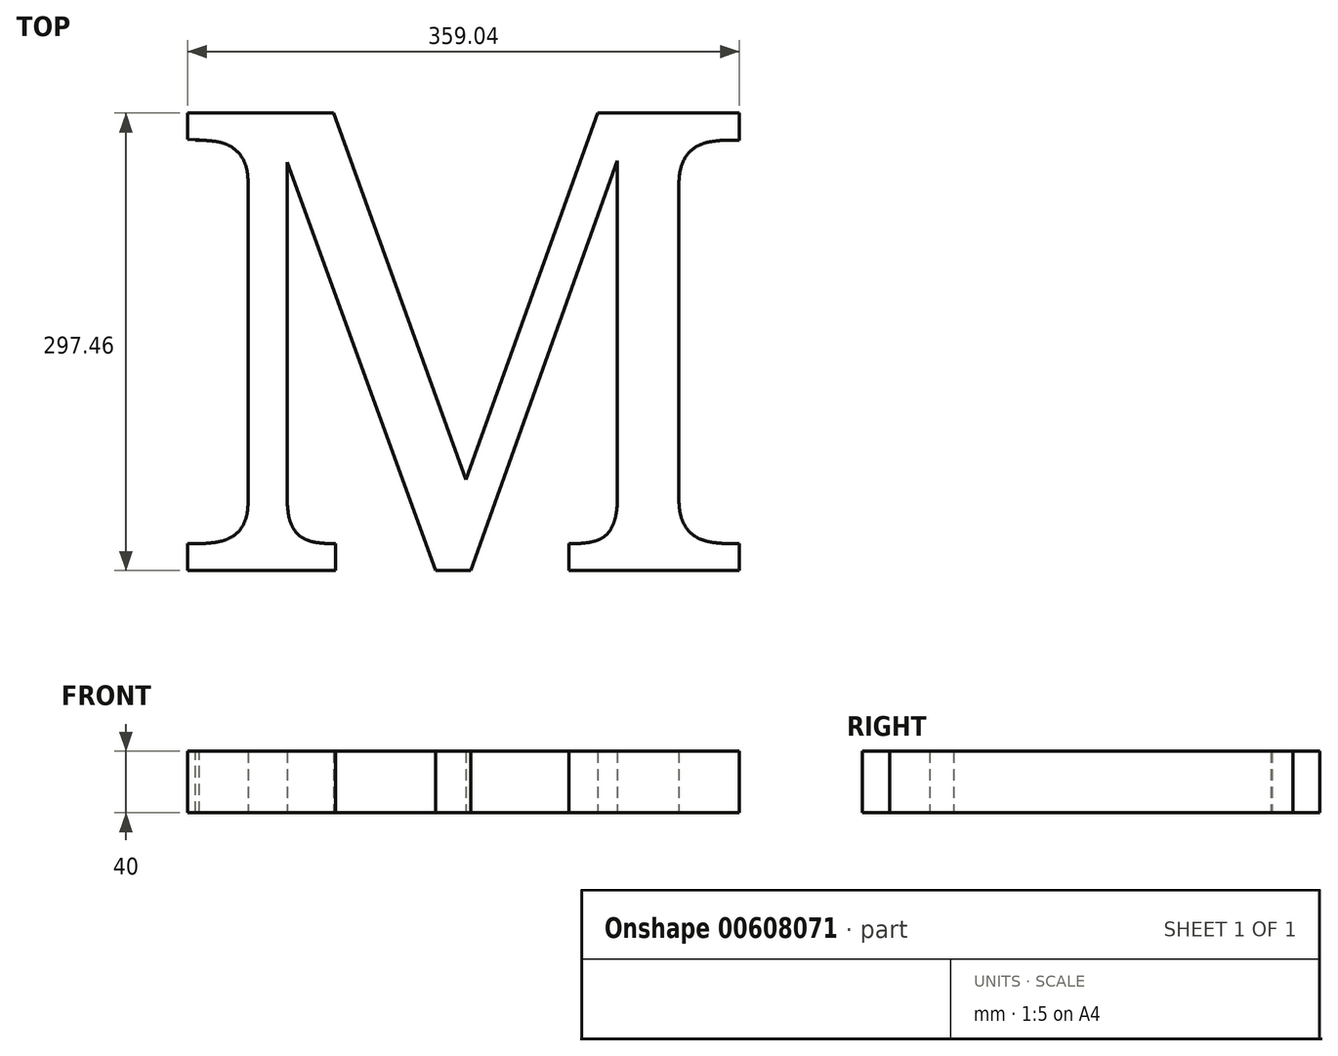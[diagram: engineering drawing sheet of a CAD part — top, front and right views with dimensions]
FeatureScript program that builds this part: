
annotation { "Feature Type Name" : "Feature", "Feature Type Description" : "" }
export const myFeature = defineFeature(function(context is Context, id is Id, definition is map)
    precondition{}
    {
        {
            var Q0;
            Q0=qCreatedBy(makeId("Top.planeOp"),FACE);
            var sketch = newSketch(context, id + "F0", { "sketchPlane" : qUnion([Q0])});
            skText(sketch, "E0", { "text": "M", "fontName": "NotoSerif-Regular.ttf"});
            const initialGuessF0  = {"E0": [-0.13929, -0.17594, 1, 0, 0.3]};
            skSetInitialGuess(sketch, initialGuessF0);
            skSolve(sketch);
        }
        {
            var Q0;
            Q0=makeQuery(id+"F0.imprint","IMPRINT",FACE,{"disambiguationData":[TD([[makeQuery(id+"F0.imprint","IMPRINT",EDGE,{"derivedFrom":sQuery(id+"F0.wireOp",EDGE,"E0.sketch_text.stroke-0")}),-1.0]])]});
            extrude(context, id + "F1", {"entities" : qUnion([Q0]), "depth" : 40 * mm, "offsetDistance" : 25 * mm});
        }
        {
            var Q0;
            Q0=makeQuery(id+"F1.opExtrude","CAP_FACE",FACE,{"disambiguationData":[OSD([sQuery(id+"F0.wireOp",EDGE,"E0.sketch_text.stroke-0"),sQuery(id+"F0.wireOp",EDGE,"E0.sketch_text.stroke-1"),sQuery(id+"F0.wireOp",EDGE,"E0.sketch_text.stroke-2"),sQuery(id+"F0.wireOp",EDGE,"E0.sketch_text.stroke-3"),sQuery(id+"F0.wireOp",EDGE,"E0.sketch_text.stroke-4"),sQuery(id+"F0.wireOp",EDGE,"E0.sketch_text.stroke-5"),sQuery(id+"F0.wireOp",EDGE,"E0.sketch_text.stroke-6"),sQuery(id+"F0.wireOp",EDGE,"E0.sketch_text.stroke-7"),sQuery(id+"F0.wireOp",EDGE,"E0.sketch_text.stroke-8"),sQuery(id+"F0.wireOp",EDGE,"E0.sketch_text.stroke-9"),sQuery(id+"F0.wireOp",EDGE,"E0.sketch_text.stroke-10"),sQuery(id+"F0.wireOp",EDGE,"E0.sketch_text.stroke-11"),sQuery(id+"F0.wireOp",EDGE,"E0.sketch_text.stroke-12"),sQuery(id+"F0.wireOp",EDGE,"E0.sketch_text.stroke-13"),sQuery(id+"F0.wireOp",EDGE,"E0.sketch_text.stroke-14"),sQuery(id+"F0.wireOp",EDGE,"E0.sketch_text.stroke-15"),sQuery(id+"F0.wireOp",EDGE,"E0.sketch_text.stroke-16"),sQuery(id+"F0.wireOp",EDGE,"E0.sketch_text.stroke-17"),sQuery(id+"F0.wireOp",EDGE,"E0.sketch_text.stroke-18"),sQuery(id+"F0.wireOp",EDGE,"E0.sketch_text.stroke-19"),sQuery(id+"F0.wireOp",EDGE,"E0.sketch_text.stroke-20"),sQuery(id+"F0.wireOp",EDGE,"E0.sketch_text.stroke-21"),sQuery(id+"F0.wireOp",EDGE,"E0.sketch_text.stroke-22"),sQuery(id+"F0.wireOp",EDGE,"E0.sketch_text.stroke-23"),sQuery(id+"F0.wireOp",EDGE,"E0.sketch_text.stroke-24"),sQuery(id+"F0.wireOp",EDGE,"E0.sketch_text.stroke-25"),sQuery(id+"F0.wireOp",EDGE,"E0.sketch_text.stroke-26"),sQuery(id+"F0.wireOp",EDGE,"E0.sketch_text.stroke-27"),sQuery(id+"F0.wireOp",EDGE,"E0.sketch_text.stroke-28"),sQuery(id+"F0.wireOp",EDGE,"E0.sketch_text.stroke-29"),sQuery(id+"F0.wireOp",EDGE,"E0.sketch_text.stroke-30"),sQuery(id+"F0.wireOp",EDGE,"E0.sketch_text.stroke-31"),sQuery(id+"F0.wireOp",EDGE,"E0.sketch_text.stroke-32"),sQuery(id+"F0.wireOp",EDGE,"E0.sketch_text.stroke-33"),sQuery(id+"F0.wireOp",EDGE,"E0.sketch_text.stroke-34"),sQuery(id+"F0.wireOp",EDGE,"E0.sketch_text.stroke-35"),sQuery(id+"F0.wireOp",EDGE,"E0.sketch_text.stroke-36"),sQuery(id+"F0.wireOp",EDGE,"E0.sketch_text.stroke-37"),sQuery(id+"F0.wireOp",EDGE,"E0.sketch_text.stroke-38"),sQuery(id+"F0.wireOp",EDGE,"E0.sketch_text.stroke-39"),sQuery(id+"F0.wireOp",EDGE,"E0.sketch_text.stroke-40"),sQuery(id+"F0.wireOp",EDGE,"E0.sketch_text.stroke-41"),sQuery(id+"F0.wireOp",EDGE,"E0.sketch_text.stroke-42"),sQuery(id+"F0.wireOp",EDGE,"E0.sketch_text.stroke-43"),sQuery(id+"F0.wireOp",EDGE,"E0.sketch_text.stroke-44"),sQuery(id+"F0.wireOp",EDGE,"E0.sketch_text.stroke-45"),sQuery(id+"F0.wireOp",EDGE,"E0.sketch_text.stroke-46"),sQuery(id+"F0.wireOp",EDGE,"E0.sketch_text.stroke-47"),sQuery(id+"F0.wireOp",EDGE,"E0.sketch_text.stroke-48")])],"isStart":false});
            var sketch = newSketch(context, id + "F2", { "sketchPlane" : qUnion([Q0])});
            skLineSegment(sketch, "E1", {"start": v(-111.3, 103.77) * mm, "end": v(-123.4, 104.63) * mm});
            skLineSegment(sketch, "E2", {"start": v(-123.4, 104.63) * mm, "end": v(-123.4, 104) * mm});
            skLineSegment(sketch, "E3.0", {"start": v(-118.13, 104) * mm, "end": v(-123.4, 104) * mm});
            skFitSpline(sketch, "E4.0", {"points": [v(-105, 103.1) * mm, v(-111.23, 104) * mm, v(-118.13, 104) * mm]});
            skPoint(sketch, "E5.orphan", {"position": v(-105, 103.1) * mm});
            skLineSegment(sketch, "E6", {"start": v(-123.4, -175.94) * mm, "end": v(235.65, -175.94) * mm});
            skLineSegment(sketch, "E7", {"start": v(-123.4, 121.52) * mm, "end": v(235.65, 121.52) * mm});
            skLineSegment(sketch, "E8", {"start": v(56.12, 121.52) * mm, "end": v(56.12, 92.45) * mm});
            skLineSegment(sketch, "E9.MirrorCS", {"start": v(235.65, 104.63) * mm, "end": v(235.65, 104) * mm});
            skLineSegment(sketch, "E10.MirrorCS", {"start": v(223.55, 103.77) * mm, "end": v(235.65, 104.63) * mm});
            skLineSegment(sketch, "E11.MirrorCS", {"start": v(230.38, 104) * mm, "end": v(235.65, 104) * mm});
            skFitSpline(sketch, "E12.MirrorCS", {"points": [v(217.26, 103.1) * mm, v(223.47, 104) * mm, v(230.38, 104) * mm]});
            skSolve(sketch);
        }
        {
            var Q0;
            Q0=makeQuery(id+"F2.imprint","IMPRINT",FACE,{"disambiguationData":[TD([[makeQuery(id+"F2.imprint","IMPRINT",EDGE,{"derivedFrom":sQuery(id+"F2.wireOp",EDGE,"E9.MirrorCS")}),-1.0]])]});
            var Q1;
            Q1=makeQuery(id+"F2.imprint","IMPRINT",FACE,{"disambiguationData":[TD([[makeQuery(id+"F2.imprint","IMPRINT",EDGE,{"derivedFrom":sQuery(id+"F2.wireOp",EDGE,"E1")}),1.0]])]});
            extrude(context, id + "F3", {"entities" : qUnion([Q0, Q1]), "operationType" : NewBodyOperationType.REMOVE, "oppositeDirection" : true, "depth" : 50 * mm, "offsetDistance" : 25 * mm});
        }
    });
